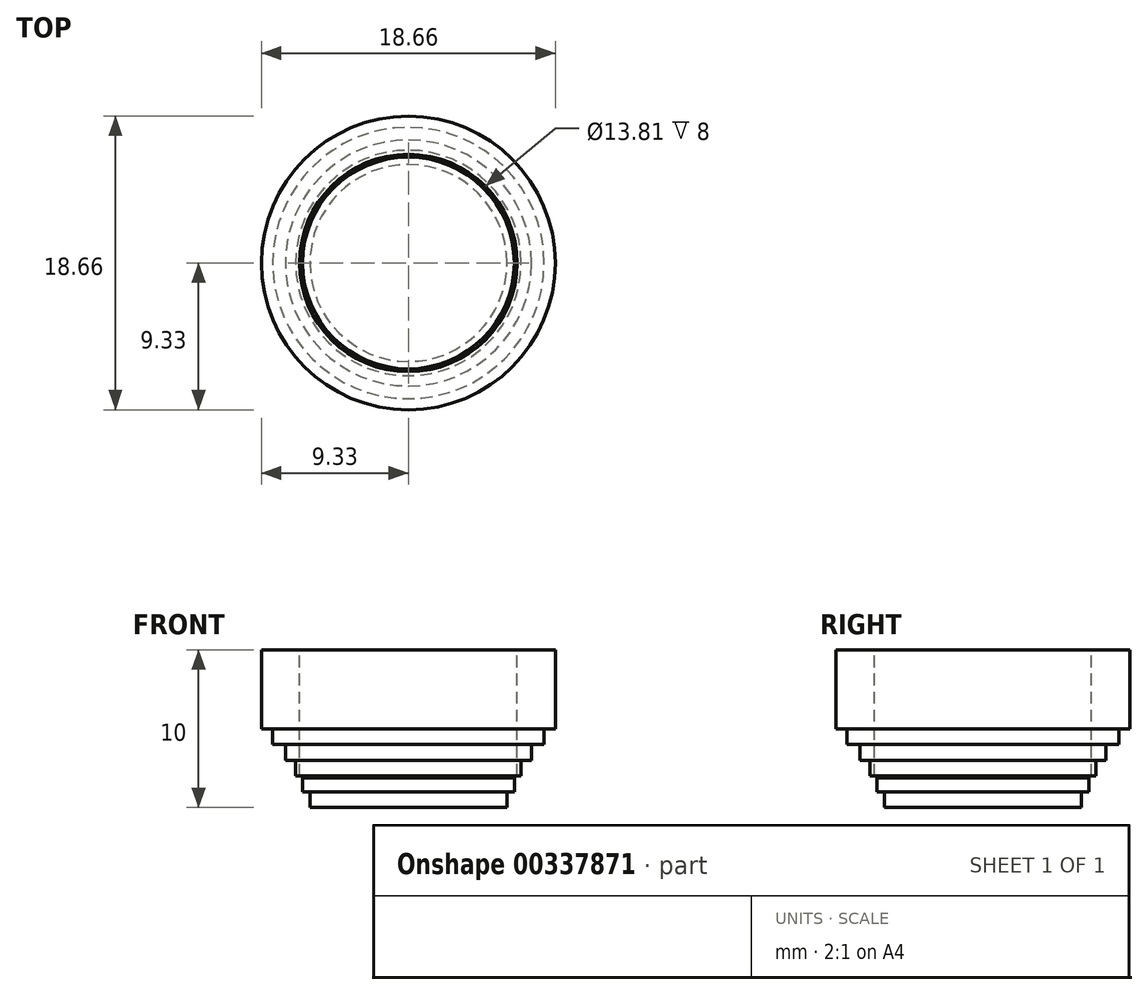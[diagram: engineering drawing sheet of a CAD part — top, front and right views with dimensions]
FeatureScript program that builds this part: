
annotation { "Feature Type Name" : "Feature", "Feature Type Description" : "" }
export const myFeature = defineFeature(function(context is Context, id is Id, definition is map)
    precondition{}
    {
        {
            var Q0;
            Q0=qCreatedBy(makeId("Top.planeOp"),FACE);
            var sketch = newSketch(context, id + "F0", { "sketchPlane" : qUnion([Q0])});
            skCircle(sketch, "E0", {"center": v(0, 0) * mm, "radius": 6.26 * mm});
            skSolve(sketch);
        }
        {
            var Q0;
            Q0 = qSketchRegion(id + "F0", true);
            extrude(context, id + "F1", {"entities" : qUnion([Q0]), "depth" : 1 * mm});
        }
        {
            var Q0;
            Q0=makeQuery(id+"F1.opExtrude","CAP_FACE",FACE,{"disambiguationData":[OSD([sQuery(id+"F0.wireOp",EDGE,"E0")])],"isStart":false});
            var sketch = newSketch(context, id + "F2", { "sketchPlane" : qUnion([Q0])});
            skCircle(sketch, "E1", {"center": v(0, 0) * mm, "radius": 6.72 * mm});
            skSolve(sketch);
        }
        {
            var Q0;
            Q0 = qSketchRegion(id + "F2", true);
            extrude(context, id + "F3", {"entities" : qUnion([Q0]), "operationType" : NewBodyOperationType.ADD, "depth" : 1 * mm});
        }
        {
            var Q0;
            Q0=makeQuery(id+"F3.opExtrude","CAP_FACE",FACE,{"disambiguationData":[OSD([sQuery(id+"F2.wireOp",EDGE,"E1")])],"isStart":false});
            var sketch = newSketch(context, id + "F4", { "sketchPlane" : qUnion([Q0])});
            skCircle(sketch, "E2", {"center": v(0, 0) * mm, "radius": 7.16 * mm});
            skSolve(sketch);
        }
        {
            var Q0;
            Q0 = qSketchRegion(id + "F4", true);
            extrude(context, id + "F5", {"entities" : qUnion([Q0]), "operationType" : NewBodyOperationType.ADD, "depth" : 1 * mm});
        }
        {
            var Q0;
            Q0=makeQuery(id+"F5.opExtrude","CAP_FACE",FACE,{"disambiguationData":[OSD([sQuery(id+"F4.wireOp",EDGE,"E2")])],"isStart":false});
            var sketch = newSketch(context, id + "F6", { "sketchPlane" : qUnion([Q0])});
            skCircle(sketch, "E3", {"center": v(0, 0) * mm, "radius": 7.81 * mm});
            skSolve(sketch);
        }
        {
            var Q0;
            Q0 = qSketchRegion(id + "F6", true);
            extrude(context, id + "F7", {"entities" : qUnion([Q0]), "operationType" : NewBodyOperationType.ADD, "depth" : 1 * mm});
        }
        {
            var Q0;
            Q0=makeQuery(id+"F7.opExtrude","CAP_FACE",FACE,{"disambiguationData":[OSD([sQuery(id+"F6.wireOp",EDGE,"E3")])],"isStart":false});
            var sketch = newSketch(context, id + "F8", { "sketchPlane" : qUnion([Q0])});
            skCircle(sketch, "E4", {"center": v(0, 0) * mm, "radius": 8.62 * mm});
            skSolve(sketch);
        }
        {
            var Q0;
            Q0 = qSketchRegion(id + "F8", true);
            extrude(context, id + "F9", {"entities" : qUnion([Q0]), "operationType" : NewBodyOperationType.ADD, "depth" : 1 * mm});
        }
        {
            var Q0;
            Q0=makeQuery(id+"F9.opExtrude","CAP_FACE",FACE,{"disambiguationData":[OSD([sQuery(id+"F8.wireOp",EDGE,"E4")])],"isStart":false});
            var sketch = newSketch(context, id + "F10", { "sketchPlane" : qUnion([Q0])});
            skCircle(sketch, "E5", {"center": v(0, 0) * mm, "radius": 9.33 * mm});
            skSolve(sketch);
        }
        {
            var Q0;
            Q0 = qSketchRegion(id + "F10", true);
            extrude(context, id + "F11", {"entities" : qUnion([Q0]), "operationType" : NewBodyOperationType.ADD, "depth" : 5 * mm});
        }
        {
            var Q0;
            Q0=makeQuery(id+"F11.opExtrude","CAP_FACE",FACE,{"disambiguationData":[OSD([sQuery(id+"F10.wireOp",EDGE,"E5")])],"isStart":false});
            var sketch = newSketch(context, id + "F12", { "sketchPlane" : qUnion([Q0])});
            skCircle(sketch, "E6", {"center": v(0, 0) * mm, "radius": 6.9 * mm});
            skSolve(sketch);
        }
        {
            var Q0;
            Q0 = qSketchRegion(id + "F12", true);
            extrude(context, id + "F13", {"entities" : qUnion([Q0]), "operationType" : NewBodyOperationType.REMOVE, "oppositeDirection" : true, "depth" : 8.13 * mm});
        }
    });
